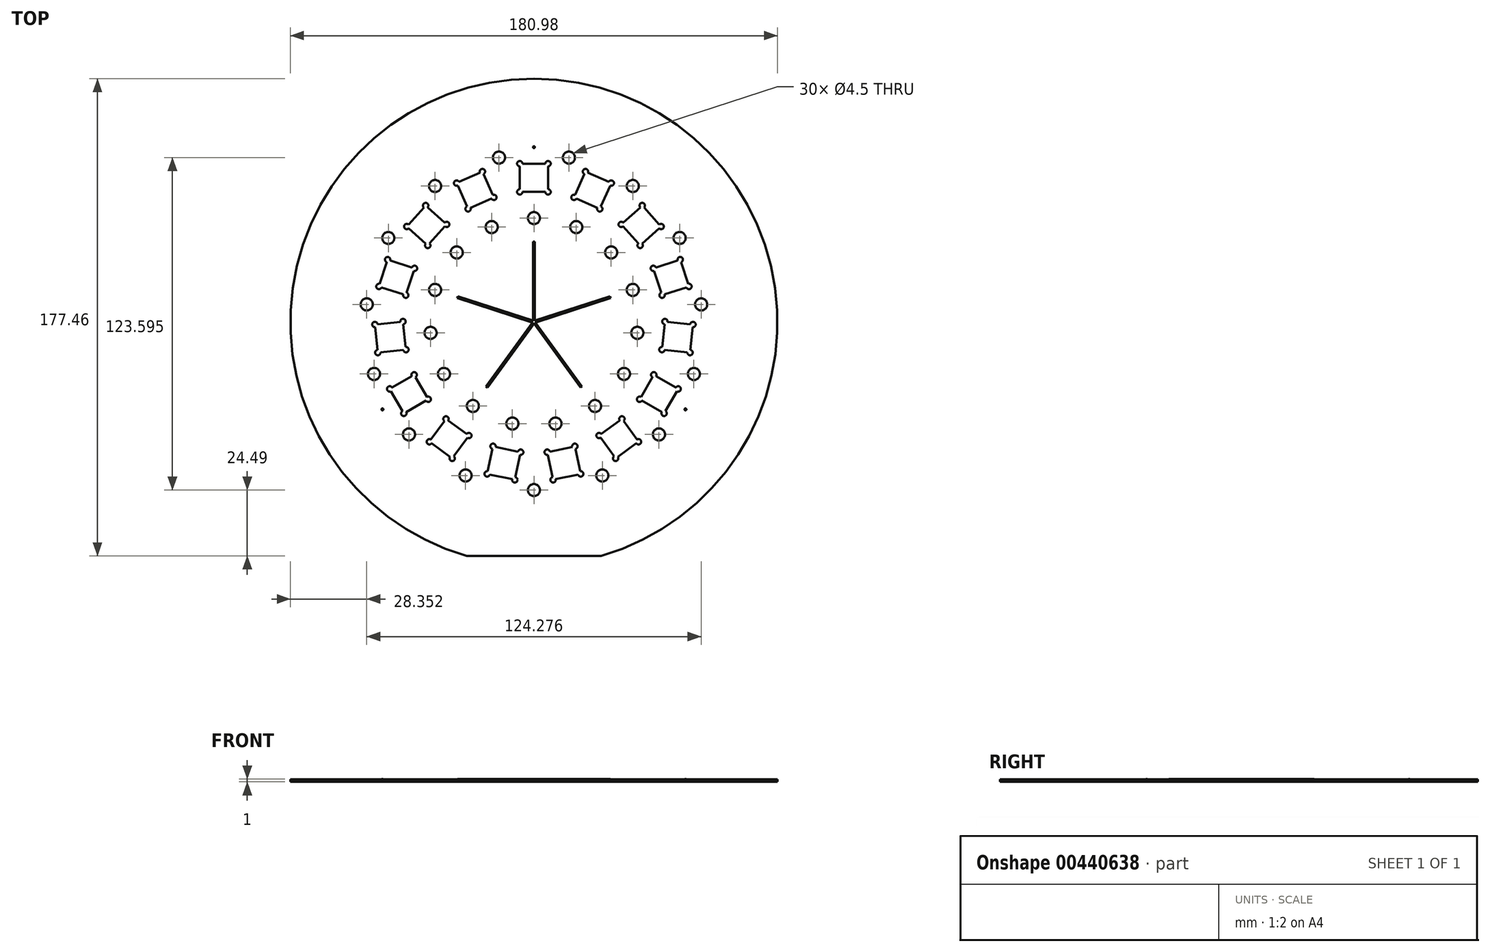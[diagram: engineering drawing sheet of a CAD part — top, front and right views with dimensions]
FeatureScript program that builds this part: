
annotation { "Feature Type Name" : "Feature", "Feature Type Description" : "" }
export const myFeature = defineFeature(function(context is Context, id is Id, definition is map)
    precondition{}
    {
        {
            var Q0;
            Q0=qCreatedBy(makeId("Top.planeOp"),FACE);
            var sketch = newSketch(context, id + "F0", { "sketchPlane" : qUnion([Q0])});
            skArc(sketch, "E0", {"start": v(25, -86.97) * mm, "mid": v(0, 90.49) * mm, "end": v(-25, -86.97) * mm});
            skCircle(sketch, "E1", {"center": v(0, 0) * mm, "radius": 53.61 * mm, "construction": true});
            skLineSegment(sketch, "E2.bottom", {"start": v(5.25, 58.86) * mm, "end": v(-5.25, 58.86) * mm});
            skLineSegment(sketch, "E2.top", {"start": v(5.25, 48.36) * mm, "end": v(-5.25, 48.36) * mm});
            skLineSegment(sketch, "E2.left", {"start": v(5.25, 58.86) * mm, "end": v(5.25, 48.36) * mm});
            skLineSegment(sketch, "E2.right", {"start": v(-5.25, 58.86) * mm, "end": v(-5.25, 48.36) * mm});
            skPoint(sketch, "E2.middle", {"position": v(0, 53.61) * mm});
            skCircle(sketch, "E3", {"center": v(0, 38.61) * mm, "radius": 2.25 * mm});
            skLineSegment(sketch, "E4", {"start": v(0, 38.61) * mm, "end": v(0, 53.61) * mm, "construction": true});
            skCircle(sketch, "E5.1.0", {"center": v(13, 61.11) * mm, "radius": 2.25 * mm, "construction": true});
            skCircle(sketch, "E5.2.0", {"center": v(-13, 61.11) * mm, "radius": 2.25 * mm});
            skCircle(sketch, "E6", {"center": v(-5.25, 58.86) * mm, "radius": 1 * mm});
            skCircle(sketch, "E7", {"center": v(5.25, 58.86) * mm, "radius": 1 * mm});
            skCircle(sketch, "E8", {"center": v(5.25, 48.36) * mm, "radius": 1 * mm});
            skCircle(sketch, "E9", {"center": v(-5.25, 48.36) * mm, "radius": 1 * mm});
            skLineSegment(sketch, "E10.1.0", {"start": v(-19.15, 55.91) * mm, "end": v(-14.88, 46.32) * mm});
            skLineSegment(sketch, "E10.1.1", {"start": v(-28.74, 51.64) * mm, "end": v(-24.47, 42.05) * mm});
            skPoint(sketch, "E10.1.2", {"position": v(-21.8, 48.98) * mm});
            skCircle(sketch, "E10.1.3", {"center": v(-15.7, 35.28) * mm, "radius": 2.25 * mm});
            skLineSegment(sketch, "E10.1.4", {"start": v(-14.88, 46.32) * mm, "end": v(-24.47, 42.05) * mm});
            skCircle(sketch, "E10.1.5", {"center": v(-13, 61.11) * mm, "radius": 2.25 * mm, "construction": true});
            skLineSegment(sketch, "E10.1.6", {"start": v(-15.7, 35.28) * mm, "end": v(-21.8, 48.98) * mm, "construction": true});
            skCircle(sketch, "E10.1.7", {"center": v(-36.72, 50.55) * mm, "radius": 2.25 * mm});
            skLineSegment(sketch, "E10.1.8", {"start": v(-19.15, 55.91) * mm, "end": v(-28.74, 51.64) * mm});
            skPoint(sketch, "E10.1.9", {"position": v(-21.8, 48.98) * mm});
            skCircle(sketch, "E10.1.10", {"center": v(-19.15, 55.91) * mm, "radius": 1 * mm});
            skCircle(sketch, "E10.1.11", {"center": v(-14.88, 46.32) * mm, "radius": 1 * mm});
            skCircle(sketch, "E10.1.12", {"center": v(-24.47, 42.05) * mm, "radius": 1 * mm});
            skCircle(sketch, "E10.1.13", {"center": v(-28.74, 51.64) * mm, "radius": 1 * mm});
            skLineSegment(sketch, "E10.2.0", {"start": v(-40.23, 43.29) * mm, "end": v(-32.43, 36.26) * mm});
            skLineSegment(sketch, "E10.2.1", {"start": v(-47.26, 35.49) * mm, "end": v(-39.46, 28.46) * mm});
            skPoint(sketch, "E10.2.2", {"position": v(-39.84, 35.88) * mm});
            skCircle(sketch, "E10.2.3", {"center": v(-28.7, 25.84) * mm, "radius": 2.25 * mm});
            skLineSegment(sketch, "E10.2.4", {"start": v(-32.43, 36.26) * mm, "end": v(-39.46, 28.46) * mm});
            skCircle(sketch, "E10.2.5", {"center": v(-36.72, 50.55) * mm, "radius": 2.25 * mm, "construction": true});
            skLineSegment(sketch, "E10.2.6", {"start": v(-28.7, 25.84) * mm, "end": v(-39.84, 35.88) * mm, "construction": true});
            skCircle(sketch, "E10.2.7", {"center": v(-54.1, 31.24) * mm, "radius": 2.25 * mm});
            skLineSegment(sketch, "E10.2.8", {"start": v(-40.23, 43.29) * mm, "end": v(-47.26, 35.49) * mm});
            skPoint(sketch, "E10.2.9", {"position": v(-39.84, 35.88) * mm});
            skCircle(sketch, "E10.2.10", {"center": v(-40.23, 43.29) * mm, "radius": 1 * mm});
            skCircle(sketch, "E10.2.11", {"center": v(-32.43, 36.26) * mm, "radius": 1 * mm});
            skCircle(sketch, "E10.2.12", {"center": v(-39.46, 28.46) * mm, "radius": 1 * mm});
            skCircle(sketch, "E10.2.13", {"center": v(-47.26, 35.49) * mm, "radius": 1 * mm});
            skLineSegment(sketch, "E11.3.3.0", {"start": v(-57.6, 13.2) * mm, "end": v(-47.62, 9.95) * mm});
            skPoint(sketch, "E11.6.3.0", {"position": v(-51, 16.57) * mm});
            skCircle(sketch, "E11.7.3.0", {"center": v(-36.72, 11.93) * mm, "radius": 2.25 * mm});
            skLineSegment(sketch, "E11.8.3.0", {"start": v(-54.36, 23.18) * mm, "end": v(-44.38, 19.94) * mm});
            skLineSegment(sketch, "E11.9.3.0", {"start": v(-44.38, 19.94) * mm, "end": v(-47.62, 9.95) * mm});
            skCircle(sketch, "E11.12.3.0", {"center": v(-54.1, 31.24) * mm, "radius": 2.25 * mm, "construction": true});
            skLineSegment(sketch, "E11.14.3.0", {"start": v(-36.72, 11.93) * mm, "end": v(-51, 16.57) * mm, "construction": true});
            skCircle(sketch, "E11.17.3.0", {"center": v(-62.14, 6.53) * mm, "radius": 2.25 * mm});
            skLineSegment(sketch, "E11.19.3.0", {"start": v(-54.36, 23.18) * mm, "end": v(-57.6, 13.2) * mm});
            skPoint(sketch, "E11.22.3.0", {"position": v(-51, 16.57) * mm});
            skCircle(sketch, "E11.23.3.0", {"center": v(-54.36, 23.18) * mm, "radius": 1 * mm});
            skCircle(sketch, "E11.25.3.0", {"center": v(-44.38, 19.94) * mm, "radius": 1 * mm});
            skCircle(sketch, "E11.27.3.0", {"center": v(-47.62, 9.95) * mm, "radius": 1 * mm});
            skCircle(sketch, "E11.29.3.0", {"center": v(-57.6, 13.2) * mm, "radius": 1 * mm});
            skLineSegment(sketch, "E11.3.4.0", {"start": v(-58, -11.37) * mm, "end": v(-47.55, -10.28) * mm});
            skPoint(sketch, "E11.6.4.0", {"position": v(-53.32, -5.6) * mm});
            skCircle(sketch, "E11.7.4.0", {"center": v(-38.4, -4.04) * mm, "radius": 2.25 * mm});
            skLineSegment(sketch, "E11.8.4.0", {"start": v(-59.1, -0.93) * mm, "end": v(-48.65, 0.17) * mm});
            skLineSegment(sketch, "E11.9.4.0", {"start": v(-48.65, 0.17) * mm, "end": v(-47.55, -10.28) * mm});
            skCircle(sketch, "E11.12.4.0", {"center": v(-62.14, 6.53) * mm, "radius": 2.25 * mm, "construction": true});
            skLineSegment(sketch, "E11.14.4.0", {"start": v(-38.4, -4.04) * mm, "end": v(-53.32, -5.6) * mm, "construction": true});
            skCircle(sketch, "E11.17.4.0", {"center": v(-59.42, -19.3) * mm, "radius": 2.25 * mm});
            skLineSegment(sketch, "E11.19.4.0", {"start": v(-59.1, -0.93) * mm, "end": v(-58, -11.37) * mm});
            skPoint(sketch, "E11.22.4.0", {"position": v(-53.32, -5.6) * mm});
            skCircle(sketch, "E11.23.4.0", {"center": v(-59.1, -0.93) * mm, "radius": 1 * mm});
            skCircle(sketch, "E11.25.4.0", {"center": v(-48.65, 0.17) * mm, "radius": 1 * mm});
            skCircle(sketch, "E11.27.4.0", {"center": v(-47.55, -10.28) * mm, "radius": 1 * mm});
            skCircle(sketch, "E11.29.4.0", {"center": v(-58, -11.37) * mm, "radius": 1 * mm});
            skLineSegment(sketch, "E11.3.5.0", {"start": v(-48.35, -33.98) * mm, "end": v(-39.26, -28.73) * mm});
            skPoint(sketch, "E11.6.5.0", {"position": v(-46.43, -26.8) * mm});
            skCircle(sketch, "E11.7.5.0", {"center": v(-33.44, -19.3) * mm, "radius": 2.25 * mm});
            skLineSegment(sketch, "E11.8.5.0", {"start": v(-53.6, -24.89) * mm, "end": v(-44.51, -19.64) * mm});
            skLineSegment(sketch, "E11.9.5.0", {"start": v(-44.51, -19.64) * mm, "end": v(-39.26, -28.73) * mm});
            skCircle(sketch, "E11.12.5.0", {"center": v(-59.42, -19.3) * mm, "radius": 2.25 * mm, "construction": true});
            skLineSegment(sketch, "E11.14.5.0", {"start": v(-33.44, -19.3) * mm, "end": v(-46.43, -26.8) * mm, "construction": true});
            skCircle(sketch, "E11.17.5.0", {"center": v(-46.43, -41.8) * mm, "radius": 2.25 * mm});
            skLineSegment(sketch, "E11.19.5.0", {"start": v(-53.6, -24.89) * mm, "end": v(-48.35, -33.98) * mm});
            skPoint(sketch, "E11.22.5.0", {"position": v(-46.43, -26.8) * mm});
            skCircle(sketch, "E11.23.5.0", {"center": v(-53.6, -24.89) * mm, "radius": 1 * mm});
            skCircle(sketch, "E11.25.5.0", {"center": v(-44.51, -19.64) * mm, "radius": 1 * mm});
            skCircle(sketch, "E11.27.5.0", {"center": v(-39.26, -28.73) * mm, "radius": 1 * mm});
            skCircle(sketch, "E11.29.5.0", {"center": v(-48.35, -33.98) * mm, "radius": 1 * mm});
            skLineSegment(sketch, "E11.3.6.0", {"start": v(-30.35, -50.7) * mm, "end": v(-24.18, -42.21) * mm});
            skPoint(sketch, "E11.6.6.0", {"position": v(-31.51, -43.38) * mm});
            skCircle(sketch, "E11.7.6.0", {"center": v(-22.7, -31.24) * mm, "radius": 2.25 * mm});
            skLineSegment(sketch, "E11.8.6.0", {"start": v(-38.85, -44.54) * mm, "end": v(-32.68, -36.04) * mm});
            skLineSegment(sketch, "E11.9.6.0", {"start": v(-32.68, -36.04) * mm, "end": v(-24.18, -42.21) * mm});
            skCircle(sketch, "E11.12.6.0", {"center": v(-46.43, -41.8) * mm, "radius": 2.25 * mm, "construction": true});
            skLineSegment(sketch, "E11.14.6.0", {"start": v(-22.7, -31.24) * mm, "end": v(-31.51, -43.38) * mm, "construction": true});
            skCircle(sketch, "E11.17.6.0", {"center": v(-25.41, -57.08) * mm, "radius": 2.25 * mm});
            skLineSegment(sketch, "E11.19.6.0", {"start": v(-38.85, -44.54) * mm, "end": v(-30.35, -50.7) * mm});
            skPoint(sketch, "E11.22.6.0", {"position": v(-31.51, -43.38) * mm});
            skCircle(sketch, "E11.23.6.0", {"center": v(-38.85, -44.54) * mm, "radius": 1 * mm});
            skCircle(sketch, "E11.25.6.0", {"center": v(-32.68, -36.04) * mm, "radius": 1 * mm});
            skCircle(sketch, "E11.27.6.0", {"center": v(-24.18, -42.21) * mm, "radius": 1 * mm});
            skCircle(sketch, "E11.29.6.0", {"center": v(-30.35, -50.7) * mm, "radius": 1 * mm});
            skLineSegment(sketch, "E11.3.7.0", {"start": v(-7.1, -58.67) * mm, "end": v(-4.92, -48.4) * mm});
            skPoint(sketch, "E11.6.7.0", {"position": v(-11.15, -52.44) * mm});
            skCircle(sketch, "E11.7.7.0", {"center": v(-8.03, -37.77) * mm, "radius": 2.25 * mm});
            skLineSegment(sketch, "E11.8.7.0", {"start": v(-17.37, -56.49) * mm, "end": v(-15.2, -46.22) * mm});
            skLineSegment(sketch, "E11.9.7.0", {"start": v(-15.2, -46.22) * mm, "end": v(-4.92, -48.4) * mm});
            skCircle(sketch, "E11.12.7.0", {"center": v(-25.41, -57.08) * mm, "radius": 2.25 * mm, "construction": true});
            skLineSegment(sketch, "E11.14.7.0", {"start": v(-8.03, -37.77) * mm, "end": v(-11.15, -52.44) * mm, "construction": true});
            skCircle(sketch, "E11.17.7.0", {"center": v(0, -62.48) * mm, "radius": 2.25 * mm});
            skLineSegment(sketch, "E11.19.7.0", {"start": v(-17.37, -56.49) * mm, "end": v(-7.1, -58.67) * mm});
            skPoint(sketch, "E11.22.7.0", {"position": v(-11.15, -52.44) * mm});
            skCircle(sketch, "E11.23.7.0", {"center": v(-17.37, -56.49) * mm, "radius": 1 * mm});
            skCircle(sketch, "E11.25.7.0", {"center": v(-15.2, -46.22) * mm, "radius": 1 * mm});
            skCircle(sketch, "E11.27.7.0", {"center": v(-4.92, -48.4) * mm, "radius": 1 * mm});
            skCircle(sketch, "E11.29.7.0", {"center": v(-7.1, -58.67) * mm, "radius": 1 * mm});
            skLineSegment(sketch, "E11.3.8.0", {"start": v(17.37, -56.49) * mm, "end": v(15.2, -46.22) * mm});
            skPoint(sketch, "E11.6.8.0", {"position": v(11.15, -52.44) * mm});
            skCircle(sketch, "E11.7.8.0", {"center": v(8.03, -37.77) * mm, "radius": 2.25 * mm});
            skLineSegment(sketch, "E11.8.8.0", {"start": v(7.1, -58.67) * mm, "end": v(4.92, -48.4) * mm});
            skLineSegment(sketch, "E11.9.8.0", {"start": v(4.92, -48.4) * mm, "end": v(15.2, -46.22) * mm});
            skCircle(sketch, "E11.12.8.0", {"center": v(0, -62.48) * mm, "radius": 2.25 * mm, "construction": true});
            skLineSegment(sketch, "E11.14.8.0", {"start": v(8.03, -37.77) * mm, "end": v(11.15, -52.44) * mm, "construction": true});
            skCircle(sketch, "E11.17.8.0", {"center": v(25.41, -57.08) * mm, "radius": 2.25 * mm});
            skLineSegment(sketch, "E11.19.8.0", {"start": v(7.1, -58.67) * mm, "end": v(17.37, -56.49) * mm});
            skPoint(sketch, "E11.22.8.0", {"position": v(11.15, -52.44) * mm});
            skCircle(sketch, "E11.23.8.0", {"center": v(7.1, -58.67) * mm, "radius": 1 * mm});
            skCircle(sketch, "E11.25.8.0", {"center": v(4.92, -48.4) * mm, "radius": 1 * mm});
            skCircle(sketch, "E11.27.8.0", {"center": v(15.2, -46.22) * mm, "radius": 1 * mm});
            skCircle(sketch, "E11.29.8.0", {"center": v(17.37, -56.49) * mm, "radius": 1 * mm});
            skLineSegment(sketch, "E11.3.9.0", {"start": v(38.85, -44.54) * mm, "end": v(32.68, -36.04) * mm});
            skPoint(sketch, "E11.6.9.0", {"position": v(31.51, -43.38) * mm});
            skCircle(sketch, "E11.7.9.0", {"center": v(22.7, -31.24) * mm, "radius": 2.25 * mm});
            skLineSegment(sketch, "E11.8.9.0", {"start": v(30.35, -50.7) * mm, "end": v(24.18, -42.21) * mm});
            skLineSegment(sketch, "E11.9.9.0", {"start": v(24.18, -42.21) * mm, "end": v(32.68, -36.04) * mm});
            skCircle(sketch, "E11.12.9.0", {"center": v(25.41, -57.08) * mm, "radius": 2.25 * mm, "construction": true});
            skLineSegment(sketch, "E11.14.9.0", {"start": v(22.7, -31.24) * mm, "end": v(31.51, -43.38) * mm, "construction": true});
            skCircle(sketch, "E11.17.9.0", {"center": v(46.43, -41.8) * mm, "radius": 2.25 * mm});
            skLineSegment(sketch, "E11.19.9.0", {"start": v(30.35, -50.7) * mm, "end": v(38.85, -44.54) * mm});
            skPoint(sketch, "E11.22.9.0", {"position": v(31.51, -43.38) * mm});
            skCircle(sketch, "E11.23.9.0", {"center": v(30.35, -50.7) * mm, "radius": 1 * mm});
            skCircle(sketch, "E11.25.9.0", {"center": v(24.18, -42.21) * mm, "radius": 1 * mm});
            skCircle(sketch, "E11.27.9.0", {"center": v(32.68, -36.04) * mm, "radius": 1 * mm});
            skCircle(sketch, "E11.29.9.0", {"center": v(38.85, -44.54) * mm, "radius": 1 * mm});
            skLineSegment(sketch, "E11.3.10.0", {"start": v(53.6, -24.89) * mm, "end": v(44.51, -19.64) * mm});
            skPoint(sketch, "E11.6.10.0", {"position": v(46.43, -26.8) * mm});
            skCircle(sketch, "E11.7.10.0", {"center": v(33.44, -19.3) * mm, "radius": 2.25 * mm});
            skLineSegment(sketch, "E11.8.10.0", {"start": v(48.35, -33.98) * mm, "end": v(39.26, -28.73) * mm});
            skLineSegment(sketch, "E11.9.10.0", {"start": v(39.26, -28.73) * mm, "end": v(44.51, -19.64) * mm});
            skCircle(sketch, "E11.12.10.0", {"center": v(46.43, -41.8) * mm, "radius": 2.25 * mm, "construction": true});
            skLineSegment(sketch, "E11.14.10.0", {"start": v(33.44, -19.3) * mm, "end": v(46.43, -26.8) * mm, "construction": true});
            skCircle(sketch, "E11.17.10.0", {"center": v(59.42, -19.3) * mm, "radius": 2.25 * mm});
            skLineSegment(sketch, "E11.19.10.0", {"start": v(48.35, -33.98) * mm, "end": v(53.6, -24.89) * mm});
            skPoint(sketch, "E11.22.10.0", {"position": v(46.43, -26.8) * mm});
            skCircle(sketch, "E11.23.10.0", {"center": v(48.35, -33.98) * mm, "radius": 1 * mm});
            skCircle(sketch, "E11.25.10.0", {"center": v(39.26, -28.73) * mm, "radius": 1 * mm});
            skCircle(sketch, "E11.27.10.0", {"center": v(44.51, -19.64) * mm, "radius": 1 * mm});
            skCircle(sketch, "E11.29.10.0", {"center": v(53.6, -24.89) * mm, "radius": 1 * mm});
            skLineSegment(sketch, "E11.3.11.0", {"start": v(59.1, -0.93) * mm, "end": v(48.65, 0.17) * mm});
            skPoint(sketch, "E11.6.11.0", {"position": v(53.32, -5.6) * mm});
            skCircle(sketch, "E11.7.11.0", {"center": v(38.4, -4.04) * mm, "radius": 2.25 * mm});
            skLineSegment(sketch, "E11.8.11.0", {"start": v(58, -11.37) * mm, "end": v(47.55, -10.28) * mm});
            skLineSegment(sketch, "E11.9.11.0", {"start": v(47.55, -10.28) * mm, "end": v(48.65, 0.17) * mm});
            skCircle(sketch, "E11.12.11.0", {"center": v(59.42, -19.3) * mm, "radius": 2.25 * mm, "construction": true});
            skLineSegment(sketch, "E11.14.11.0", {"start": v(38.4, -4.04) * mm, "end": v(53.32, -5.6) * mm, "construction": true});
            skCircle(sketch, "E11.17.11.0", {"center": v(62.14, 6.53) * mm, "radius": 2.25 * mm});
            skLineSegment(sketch, "E11.19.11.0", {"start": v(58, -11.37) * mm, "end": v(59.1, -0.93) * mm});
            skPoint(sketch, "E11.22.11.0", {"position": v(53.32, -5.6) * mm});
            skCircle(sketch, "E11.23.11.0", {"center": v(58, -11.37) * mm, "radius": 1 * mm});
            skCircle(sketch, "E11.25.11.0", {"center": v(47.55, -10.28) * mm, "radius": 1 * mm});
            skCircle(sketch, "E11.27.11.0", {"center": v(48.65, 0.17) * mm, "radius": 1 * mm});
            skCircle(sketch, "E11.29.11.0", {"center": v(59.1, -0.93) * mm, "radius": 1 * mm});
            skLineSegment(sketch, "E11.3.12.0", {"start": v(54.36, 23.18) * mm, "end": v(44.38, 19.94) * mm});
            skPoint(sketch, "E11.6.12.0", {"position": v(51, 16.57) * mm});
            skCircle(sketch, "E11.7.12.0", {"center": v(36.72, 11.93) * mm, "radius": 2.25 * mm});
            skLineSegment(sketch, "E11.8.12.0", {"start": v(57.6, 13.2) * mm, "end": v(47.62, 9.95) * mm});
            skLineSegment(sketch, "E11.9.12.0", {"start": v(47.62, 9.95) * mm, "end": v(44.38, 19.94) * mm});
            skCircle(sketch, "E11.12.12.0", {"center": v(62.14, 6.53) * mm, "radius": 2.25 * mm, "construction": true});
            skLineSegment(sketch, "E11.14.12.0", {"start": v(36.72, 11.93) * mm, "end": v(51, 16.57) * mm, "construction": true});
            skCircle(sketch, "E11.17.12.0", {"center": v(54.1, 31.24) * mm, "radius": 2.25 * mm});
            skLineSegment(sketch, "E11.19.12.0", {"start": v(57.6, 13.2) * mm, "end": v(54.36, 23.18) * mm});
            skPoint(sketch, "E11.22.12.0", {"position": v(51, 16.57) * mm});
            skCircle(sketch, "E11.23.12.0", {"center": v(57.6, 13.2) * mm, "radius": 1 * mm});
            skCircle(sketch, "E11.25.12.0", {"center": v(47.62, 9.95) * mm, "radius": 1 * mm});
            skCircle(sketch, "E11.27.12.0", {"center": v(44.38, 19.94) * mm, "radius": 1 * mm});
            skCircle(sketch, "E11.29.12.0", {"center": v(54.36, 23.18) * mm, "radius": 1 * mm});
            skLineSegment(sketch, "E11.3.13.0", {"start": v(40.23, 43.29) * mm, "end": v(32.43, 36.26) * mm});
            skPoint(sketch, "E11.6.13.0", {"position": v(39.84, 35.88) * mm});
            skCircle(sketch, "E11.7.13.0", {"center": v(28.7, 25.84) * mm, "radius": 2.25 * mm});
            skLineSegment(sketch, "E11.8.13.0", {"start": v(47.26, 35.49) * mm, "end": v(39.46, 28.46) * mm});
            skLineSegment(sketch, "E11.9.13.0", {"start": v(39.46, 28.46) * mm, "end": v(32.43, 36.26) * mm});
            skCircle(sketch, "E11.12.13.0", {"center": v(54.1, 31.24) * mm, "radius": 2.25 * mm, "construction": true});
            skLineSegment(sketch, "E11.14.13.0", {"start": v(28.7, 25.84) * mm, "end": v(39.84, 35.88) * mm, "construction": true});
            skCircle(sketch, "E11.17.13.0", {"center": v(36.72, 50.55) * mm, "radius": 2.25 * mm});
            skLineSegment(sketch, "E11.19.13.0", {"start": v(47.26, 35.49) * mm, "end": v(40.23, 43.29) * mm});
            skPoint(sketch, "E11.22.13.0", {"position": v(39.84, 35.88) * mm});
            skCircle(sketch, "E11.23.13.0", {"center": v(47.26, 35.49) * mm, "radius": 1 * mm});
            skCircle(sketch, "E11.25.13.0", {"center": v(39.46, 28.46) * mm, "radius": 1 * mm});
            skCircle(sketch, "E11.27.13.0", {"center": v(32.43, 36.26) * mm, "radius": 1 * mm});
            skCircle(sketch, "E11.29.13.0", {"center": v(40.23, 43.29) * mm, "radius": 1 * mm});
            skLineSegment(sketch, "E11.3.14.0", {"start": v(19.15, 55.91) * mm, "end": v(14.88, 46.32) * mm});
            skPoint(sketch, "E11.6.14.0", {"position": v(21.8, 48.98) * mm});
            skCircle(sketch, "E11.7.14.0", {"center": v(15.7, 35.28) * mm, "radius": 2.25 * mm});
            skLineSegment(sketch, "E11.8.14.0", {"start": v(28.74, 51.64) * mm, "end": v(24.47, 42.05) * mm});
            skLineSegment(sketch, "E11.9.14.0", {"start": v(24.47, 42.05) * mm, "end": v(14.88, 46.32) * mm});
            skCircle(sketch, "E11.12.14.0", {"center": v(36.72, 50.55) * mm, "radius": 2.25 * mm, "construction": true});
            skLineSegment(sketch, "E11.14.14.0", {"start": v(15.7, 35.28) * mm, "end": v(21.8, 48.98) * mm, "construction": true});
            skCircle(sketch, "E11.17.14.0", {"center": v(13, 61.11) * mm, "radius": 2.25 * mm});
            skLineSegment(sketch, "E11.19.14.0", {"start": v(28.74, 51.64) * mm, "end": v(19.15, 55.91) * mm});
            skPoint(sketch, "E11.22.14.0", {"position": v(21.8, 48.98) * mm});
            skCircle(sketch, "E11.23.14.0", {"center": v(28.74, 51.64) * mm, "radius": 1 * mm});
            skCircle(sketch, "E11.25.14.0", {"center": v(24.47, 42.05) * mm, "radius": 1 * mm});
            skCircle(sketch, "E11.27.14.0", {"center": v(14.88, 46.32) * mm, "radius": 1 * mm});
            skCircle(sketch, "E11.29.14.0", {"center": v(19.15, 55.91) * mm, "radius": 1 * mm});
            skLineSegment(sketch, "E12", {"start": v(-25, -86.97) * mm, "end": v(25, -86.97) * mm});
            skPoint(sketch, "E13.endSnap0", {"position": v(9.59, -45.1) * mm});
            skLineSegment(sketch, "E14", {"start": v(0, 0) * mm, "end": v(0, -86.97) * mm, "construction": true});
            skSolve(sketch);
        }
        {
            var Q0;
            Q0=qSketchRegion(id+"F0",true);
            extrude(context, id + "F1", {"entities" : qUnion([Q0]), "depth" : 1 * mm});
        }
        {
            var Q0;
            Q0=makeQuery(id+"F1.opExtrude","CAP_FACE",FACE,{"disambiguationData":[OSD([sQuery(id+"F0.wireOp",EDGE,"E0"),sQuery(id+"F0.wireOp",EDGE,"E2.bottom"),sQuery(id+"F0.wireOp",EDGE,"E2.top"),sQuery(id+"F0.wireOp",EDGE,"E2.left"),sQuery(id+"F0.wireOp",EDGE,"E2.right"),sQuery(id+"F0.wireOp",EDGE,"E3"),sQuery(id+"F0.wireOp",EDGE,"E5.2.0"),sQuery(id+"F0.wireOp",EDGE,"E6"),sQuery(id+"F0.wireOp",EDGE,"E7"),sQuery(id+"F0.wireOp",EDGE,"E8"),sQuery(id+"F0.wireOp",EDGE,"E9"),sQuery(id+"F0.wireOp",EDGE,"E10.1.0"),sQuery(id+"F0.wireOp",EDGE,"E10.1.1"),sQuery(id+"F0.wireOp",EDGE,"E10.1.3"),sQuery(id+"F0.wireOp",EDGE,"E10.1.4"),sQuery(id+"F0.wireOp",EDGE,"E10.1.7"),sQuery(id+"F0.wireOp",EDGE,"E10.1.8"),sQuery(id+"F0.wireOp",EDGE,"E10.1.10"),sQuery(id+"F0.wireOp",EDGE,"E10.1.11"),sQuery(id+"F0.wireOp",EDGE,"E10.1.12"),sQuery(id+"F0.wireOp",EDGE,"E10.1.13"),sQuery(id+"F0.wireOp",EDGE,"E10.2.0"),sQuery(id+"F0.wireOp",EDGE,"E10.2.1"),sQuery(id+"F0.wireOp",EDGE,"E10.2.3"),sQuery(id+"F0.wireOp",EDGE,"E10.2.4"),sQuery(id+"F0.wireOp",EDGE,"E10.2.7"),sQuery(id+"F0.wireOp",EDGE,"E10.2.8"),sQuery(id+"F0.wireOp",EDGE,"E10.2.10"),sQuery(id+"F0.wireOp",EDGE,"E10.2.11"),sQuery(id+"F0.wireOp",EDGE,"E10.2.12"),sQuery(id+"F0.wireOp",EDGE,"E10.2.13"),sQuery(id+"F0.wireOp",EDGE,"E11.3.3.0"),sQuery(id+"F0.wireOp",EDGE,"E11.7.3.0"),sQuery(id+"F0.wireOp",EDGE,"E11.8.3.0"),sQuery(id+"F0.wireOp",EDGE,"E11.9.3.0"),sQuery(id+"F0.wireOp",EDGE,"E11.17.3.0"),sQuery(id+"F0.wireOp",EDGE,"E11.19.3.0"),sQuery(id+"F0.wireOp",EDGE,"E11.23.3.0"),sQuery(id+"F0.wireOp",EDGE,"E11.25.3.0"),sQuery(id+"F0.wireOp",EDGE,"E11.27.3.0"),sQuery(id+"F0.wireOp",EDGE,"E11.29.3.0"),sQuery(id+"F0.wireOp",EDGE,"E11.3.4.0"),sQuery(id+"F0.wireOp",EDGE,"E11.7.4.0"),sQuery(id+"F0.wireOp",EDGE,"E11.8.4.0"),sQuery(id+"F0.wireOp",EDGE,"E11.9.4.0"),sQuery(id+"F0.wireOp",EDGE,"E11.17.4.0"),sQuery(id+"F0.wireOp",EDGE,"E11.19.4.0"),sQuery(id+"F0.wireOp",EDGE,"E11.23.4.0"),sQuery(id+"F0.wireOp",EDGE,"E11.25.4.0"),sQuery(id+"F0.wireOp",EDGE,"E11.27.4.0"),sQuery(id+"F0.wireOp",EDGE,"E11.29.4.0"),sQuery(id+"F0.wireOp",EDGE,"E11.3.5.0"),sQuery(id+"F0.wireOp",EDGE,"E11.7.5.0"),sQuery(id+"F0.wireOp",EDGE,"E11.8.5.0"),sQuery(id+"F0.wireOp",EDGE,"E11.9.5.0"),sQuery(id+"F0.wireOp",EDGE,"E11.17.5.0"),sQuery(id+"F0.wireOp",EDGE,"E11.19.5.0"),sQuery(id+"F0.wireOp",EDGE,"E11.23.5.0"),sQuery(id+"F0.wireOp",EDGE,"E11.25.5.0"),sQuery(id+"F0.wireOp",EDGE,"E11.27.5.0"),sQuery(id+"F0.wireOp",EDGE,"E11.29.5.0"),sQuery(id+"F0.wireOp",EDGE,"E11.3.6.0"),sQuery(id+"F0.wireOp",EDGE,"E11.7.6.0"),sQuery(id+"F0.wireOp",EDGE,"E11.8.6.0"),sQuery(id+"F0.wireOp",EDGE,"E11.9.6.0"),sQuery(id+"F0.wireOp",EDGE,"E11.17.6.0"),sQuery(id+"F0.wireOp",EDGE,"E11.19.6.0"),sQuery(id+"F0.wireOp",EDGE,"E11.23.6.0"),sQuery(id+"F0.wireOp",EDGE,"E11.25.6.0"),sQuery(id+"F0.wireOp",EDGE,"E11.27.6.0"),sQuery(id+"F0.wireOp",EDGE,"E11.29.6.0"),sQuery(id+"F0.wireOp",EDGE,"E11.3.7.0"),sQuery(id+"F0.wireOp",EDGE,"E11.7.7.0"),sQuery(id+"F0.wireOp",EDGE,"E11.8.7.0"),sQuery(id+"F0.wireOp",EDGE,"E11.9.7.0"),sQuery(id+"F0.wireOp",EDGE,"E11.17.7.0"),sQuery(id+"F0.wireOp",EDGE,"E11.19.7.0"),sQuery(id+"F0.wireOp",EDGE,"E11.23.7.0"),sQuery(id+"F0.wireOp",EDGE,"E11.25.7.0"),sQuery(id+"F0.wireOp",EDGE,"E11.27.7.0"),sQuery(id+"F0.wireOp",EDGE,"E11.29.7.0"),sQuery(id+"F0.wireOp",EDGE,"E11.3.8.0"),sQuery(id+"F0.wireOp",EDGE,"E11.7.8.0"),sQuery(id+"F0.wireOp",EDGE,"E11.8.8.0"),sQuery(id+"F0.wireOp",EDGE,"E11.9.8.0"),sQuery(id+"F0.wireOp",EDGE,"E11.17.8.0"),sQuery(id+"F0.wireOp",EDGE,"E11.19.8.0"),sQuery(id+"F0.wireOp",EDGE,"E11.23.8.0"),sQuery(id+"F0.wireOp",EDGE,"E11.25.8.0"),sQuery(id+"F0.wireOp",EDGE,"E11.27.8.0"),sQuery(id+"F0.wireOp",EDGE,"E11.29.8.0"),sQuery(id+"F0.wireOp",EDGE,"E11.3.9.0"),sQuery(id+"F0.wireOp",EDGE,"E11.7.9.0"),sQuery(id+"F0.wireOp",EDGE,"E11.8.9.0"),sQuery(id+"F0.wireOp",EDGE,"E11.9.9.0"),sQuery(id+"F0.wireOp",EDGE,"E11.17.9.0"),sQuery(id+"F0.wireOp",EDGE,"E11.19.9.0"),sQuery(id+"F0.wireOp",EDGE,"E11.23.9.0"),sQuery(id+"F0.wireOp",EDGE,"E11.25.9.0"),sQuery(id+"F0.wireOp",EDGE,"E11.27.9.0"),sQuery(id+"F0.wireOp",EDGE,"E11.29.9.0"),sQuery(id+"F0.wireOp",EDGE,"E11.3.10.0"),sQuery(id+"F0.wireOp",EDGE,"E11.7.10.0"),sQuery(id+"F0.wireOp",EDGE,"E11.8.10.0"),sQuery(id+"F0.wireOp",EDGE,"E11.9.10.0"),sQuery(id+"F0.wireOp",EDGE,"E11.17.10.0"),sQuery(id+"F0.wireOp",EDGE,"E11.19.10.0"),sQuery(id+"F0.wireOp",EDGE,"E11.23.10.0"),sQuery(id+"F0.wireOp",EDGE,"E11.25.10.0"),sQuery(id+"F0.wireOp",EDGE,"E11.27.10.0"),sQuery(id+"F0.wireOp",EDGE,"E11.29.10.0"),sQuery(id+"F0.wireOp",EDGE,"E11.3.11.0"),sQuery(id+"F0.wireOp",EDGE,"E11.7.11.0"),sQuery(id+"F0.wireOp",EDGE,"E11.8.11.0"),sQuery(id+"F0.wireOp",EDGE,"E11.9.11.0"),sQuery(id+"F0.wireOp",EDGE,"E11.17.11.0"),sQuery(id+"F0.wireOp",EDGE,"E11.19.11.0"),sQuery(id+"F0.wireOp",EDGE,"E11.23.11.0"),sQuery(id+"F0.wireOp",EDGE,"E11.25.11.0"),sQuery(id+"F0.wireOp",EDGE,"E11.27.11.0"),sQuery(id+"F0.wireOp",EDGE,"E11.29.11.0"),sQuery(id+"F0.wireOp",EDGE,"E11.3.12.0"),sQuery(id+"F0.wireOp",EDGE,"E11.7.12.0"),sQuery(id+"F0.wireOp",EDGE,"E11.8.12.0"),sQuery(id+"F0.wireOp",EDGE,"E11.9.12.0"),sQuery(id+"F0.wireOp",EDGE,"E11.17.12.0"),sQuery(id+"F0.wireOp",EDGE,"E11.19.12.0"),sQuery(id+"F0.wireOp",EDGE,"E11.23.12.0"),sQuery(id+"F0.wireOp",EDGE,"E11.25.12.0"),sQuery(id+"F0.wireOp",EDGE,"E11.27.12.0"),sQuery(id+"F0.wireOp",EDGE,"E11.29.12.0"),sQuery(id+"F0.wireOp",EDGE,"E11.3.13.0"),sQuery(id+"F0.wireOp",EDGE,"E11.7.13.0"),sQuery(id+"F0.wireOp",EDGE,"E11.8.13.0"),sQuery(id+"F0.wireOp",EDGE,"E11.9.13.0"),sQuery(id+"F0.wireOp",EDGE,"E11.17.13.0"),sQuery(id+"F0.wireOp",EDGE,"E11.19.13.0"),sQuery(id+"F0.wireOp",EDGE,"E11.23.13.0"),sQuery(id+"F0.wireOp",EDGE,"E11.25.13.0"),sQuery(id+"F0.wireOp",EDGE,"E11.27.13.0"),sQuery(id+"F0.wireOp",EDGE,"E11.29.13.0"),sQuery(id+"F0.wireOp",EDGE,"E11.3.14.0"),sQuery(id+"F0.wireOp",EDGE,"E11.7.14.0"),sQuery(id+"F0.wireOp",EDGE,"E11.8.14.0"),sQuery(id+"F0.wireOp",EDGE,"E11.9.14.0"),sQuery(id+"F0.wireOp",EDGE,"E11.17.14.0"),sQuery(id+"F0.wireOp",EDGE,"E11.19.14.0"),sQuery(id+"F0.wireOp",EDGE,"E11.23.14.0"),sQuery(id+"F0.wireOp",EDGE,"E11.25.14.0"),sQuery(id+"F0.wireOp",EDGE,"E11.27.14.0"),sQuery(id+"F0.wireOp",EDGE,"E11.29.14.0"),sQuery(id+"F0.wireOp",EDGE,"E11.3.15.0"),sQuery(id+"F0.wireOp",EDGE,"E11.7.15.0"),sQuery(id+"F0.wireOp",EDGE,"E11.8.15.0"),sQuery(id+"F0.wireOp",EDGE,"E11.9.15.0"),sQuery(id+"F0.wireOp",EDGE,"E11.17.15.0"),sQuery(id+"F0.wireOp",EDGE,"E11.19.15.0"),sQuery(id+"F0.wireOp",EDGE,"E11.23.15.0"),sQuery(id+"F0.wireOp",EDGE,"E11.25.15.0"),sQuery(id+"F0.wireOp",EDGE,"E11.27.15.0"),sQuery(id+"F0.wireOp",EDGE,"E11.29.15.0"),sQuery(id+"F0.wireOp",EDGE,"E12")])],"isStart":false});
            var sketch = newSketch(context, id + "F2", { "sketchPlane" : qUnion([Q0])});
            skLineSegment(sketch, "E15.bottom", {"start": v(-0.5, 0) * mm, "end": v(0.5, 0) * mm});
            skLineSegment(sketch, "E15.top", {"start": v(-0.5, 30) * mm, "end": v(0.5, 30) * mm});
            skLineSegment(sketch, "E15.left", {"start": v(-0.5, 0) * mm, "end": v(-0.5, 30) * mm});
            skLineSegment(sketch, "E15.right", {"start": v(0.5, 0) * mm, "end": v(0.5, 30) * mm});
            skLineSegment(sketch, "E16.1.0", {"start": v(-0.15, -0.48) * mm, "end": v(-28.69, 8.8) * mm});
            skLineSegment(sketch, "E16.1.1", {"start": v(0.15, 0.48) * mm, "end": v(-28.38, 9.75) * mm});
            skLineSegment(sketch, "E16.1.2", {"start": v(-0.15, -0.48) * mm, "end": v(0.15, 0.48) * mm});
            skLineSegment(sketch, "E16.1.3", {"start": v(-28.69, 8.8) * mm, "end": v(-28.38, 9.75) * mm});
            skLineSegment(sketch, "E16.2.0", {"start": v(0.4, -0.3) * mm, "end": v(-17.23, -24.56) * mm});
            skLineSegment(sketch, "E16.2.1", {"start": v(-0.4, 0.3) * mm, "end": v(-18.04, -23.98) * mm});
            skLineSegment(sketch, "E16.2.2", {"start": v(0.4, -0.3) * mm, "end": v(-0.4, 0.3) * mm});
            skLineSegment(sketch, "E16.2.3", {"start": v(-17.23, -24.56) * mm, "end": v(-18.04, -23.98) * mm});
            skPoint(sketch, "E16.center", {"position": v(0, 0) * mm});
            skLineSegment(sketch, "E17.1.3.0", {"start": v(0.4, 0.3) * mm, "end": v(18.04, -23.98) * mm});
            skLineSegment(sketch, "E17.3.3.0", {"start": v(-0.4, -0.3) * mm, "end": v(17.23, -24.56) * mm});
            skLineSegment(sketch, "E17.6.3.0", {"start": v(0.4, 0.3) * mm, "end": v(-0.4, -0.3) * mm});
            skLineSegment(sketch, "E17.9.3.0", {"start": v(18.04, -23.98) * mm, "end": v(17.23, -24.56) * mm});
            skLineSegment(sketch, "E18.1.4.0", {"start": v(-0.15, 0.48) * mm, "end": v(28.38, 9.75) * mm});
            skLineSegment(sketch, "E18.3.4.0", {"start": v(0.15, -0.48) * mm, "end": v(28.69, 8.8) * mm});
            skLineSegment(sketch, "E18.6.4.0", {"start": v(-0.15, 0.48) * mm, "end": v(0.15, -0.48) * mm});
            skLineSegment(sketch, "E18.9.4.0", {"start": v(28.38, 9.75) * mm, "end": v(28.69, 8.8) * mm});
            skCircle(sketch, "E19", {"center": v(0, 65) * mm, "radius": 0.5 * mm});
            skCircle(sketch, "E20.1.0", {"center": v(-56.3, -32.5) * mm, "radius": 0.5 * mm});
            skCircle(sketch, "E20.2.0", {"center": v(56.3, -32.5) * mm, "radius": 0.5 * mm});
            skSolve(sketch);
        }
        {
            var Q0;
            {var subQ15=sQuery(id+"F2.wireOp",EDGE,"E15.top");Q0=makeQuery(id+"F2.imprint","IMPRINT",FACE,{"disambiguationData":[TD([[makeQuery(id+"F2.imprint","IMPRINT",EDGE,{"derivedFrom":subQ15}),1.0]])]});}
            extrude(context, id + "F3", {"entities" : qUnion([Q0]), "operationType" : NewBodyOperationType.REMOVE, "oppositeDirection" : true, "depth" : .1 * mm});
        }
        {
            var Q0;
            Q0=makeQuery(id+"F1.opExtrude","CAP_FACE",FACE,{"disambiguationData":[OSD([sQuery(id+"F0.wireOp",EDGE,"E0"),sQuery(id+"F0.wireOp",EDGE,"E2.bottom"),sQuery(id+"F0.wireOp",EDGE,"E2.top"),sQuery(id+"F0.wireOp",EDGE,"E2.left"),sQuery(id+"F0.wireOp",EDGE,"E2.right"),sQuery(id+"F0.wireOp",EDGE,"E3"),sQuery(id+"F0.wireOp",EDGE,"E5.2.0"),sQuery(id+"F0.wireOp",EDGE,"E6"),sQuery(id+"F0.wireOp",EDGE,"E7"),sQuery(id+"F0.wireOp",EDGE,"E8"),sQuery(id+"F0.wireOp",EDGE,"E9"),sQuery(id+"F0.wireOp",EDGE,"E10.1.0"),sQuery(id+"F0.wireOp",EDGE,"E10.1.1"),sQuery(id+"F0.wireOp",EDGE,"E10.1.3"),sQuery(id+"F0.wireOp",EDGE,"E10.1.4"),sQuery(id+"F0.wireOp",EDGE,"E10.1.7"),sQuery(id+"F0.wireOp",EDGE,"E10.1.8"),sQuery(id+"F0.wireOp",EDGE,"E10.1.10"),sQuery(id+"F0.wireOp",EDGE,"E10.1.11"),sQuery(id+"F0.wireOp",EDGE,"E10.1.12"),sQuery(id+"F0.wireOp",EDGE,"E10.1.13"),sQuery(id+"F0.wireOp",EDGE,"E10.2.0"),sQuery(id+"F0.wireOp",EDGE,"E10.2.1"),sQuery(id+"F0.wireOp",EDGE,"E10.2.3"),sQuery(id+"F0.wireOp",EDGE,"E10.2.4"),sQuery(id+"F0.wireOp",EDGE,"E10.2.7"),sQuery(id+"F0.wireOp",EDGE,"E10.2.8"),sQuery(id+"F0.wireOp",EDGE,"E10.2.10"),sQuery(id+"F0.wireOp",EDGE,"E10.2.11"),sQuery(id+"F0.wireOp",EDGE,"E10.2.12"),sQuery(id+"F0.wireOp",EDGE,"E10.2.13"),sQuery(id+"F0.wireOp",EDGE,"E11.3.3.0"),sQuery(id+"F0.wireOp",EDGE,"E11.7.3.0"),sQuery(id+"F0.wireOp",EDGE,"E11.8.3.0"),sQuery(id+"F0.wireOp",EDGE,"E11.9.3.0"),sQuery(id+"F0.wireOp",EDGE,"E11.17.3.0"),sQuery(id+"F0.wireOp",EDGE,"E11.19.3.0"),sQuery(id+"F0.wireOp",EDGE,"E11.23.3.0"),sQuery(id+"F0.wireOp",EDGE,"E11.25.3.0"),sQuery(id+"F0.wireOp",EDGE,"E11.27.3.0"),sQuery(id+"F0.wireOp",EDGE,"E11.29.3.0"),sQuery(id+"F0.wireOp",EDGE,"E11.3.4.0"),sQuery(id+"F0.wireOp",EDGE,"E11.7.4.0"),sQuery(id+"F0.wireOp",EDGE,"E11.8.4.0"),sQuery(id+"F0.wireOp",EDGE,"E11.9.4.0"),sQuery(id+"F0.wireOp",EDGE,"E11.17.4.0"),sQuery(id+"F0.wireOp",EDGE,"E11.19.4.0"),sQuery(id+"F0.wireOp",EDGE,"E11.23.4.0"),sQuery(id+"F0.wireOp",EDGE,"E11.25.4.0"),sQuery(id+"F0.wireOp",EDGE,"E11.27.4.0"),sQuery(id+"F0.wireOp",EDGE,"E11.29.4.0"),sQuery(id+"F0.wireOp",EDGE,"E11.3.5.0"),sQuery(id+"F0.wireOp",EDGE,"E11.7.5.0"),sQuery(id+"F0.wireOp",EDGE,"E11.8.5.0"),sQuery(id+"F0.wireOp",EDGE,"E11.9.5.0"),sQuery(id+"F0.wireOp",EDGE,"E11.17.5.0"),sQuery(id+"F0.wireOp",EDGE,"E11.19.5.0"),sQuery(id+"F0.wireOp",EDGE,"E11.23.5.0"),sQuery(id+"F0.wireOp",EDGE,"E11.25.5.0"),sQuery(id+"F0.wireOp",EDGE,"E11.27.5.0"),sQuery(id+"F0.wireOp",EDGE,"E11.29.5.0"),sQuery(id+"F0.wireOp",EDGE,"E11.3.6.0"),sQuery(id+"F0.wireOp",EDGE,"E11.7.6.0"),sQuery(id+"F0.wireOp",EDGE,"E11.8.6.0"),sQuery(id+"F0.wireOp",EDGE,"E11.9.6.0"),sQuery(id+"F0.wireOp",EDGE,"E11.17.6.0"),sQuery(id+"F0.wireOp",EDGE,"E11.19.6.0"),sQuery(id+"F0.wireOp",EDGE,"E11.23.6.0"),sQuery(id+"F0.wireOp",EDGE,"E11.25.6.0"),sQuery(id+"F0.wireOp",EDGE,"E11.27.6.0"),sQuery(id+"F0.wireOp",EDGE,"E11.29.6.0"),sQuery(id+"F0.wireOp",EDGE,"E11.3.7.0"),sQuery(id+"F0.wireOp",EDGE,"E11.7.7.0"),sQuery(id+"F0.wireOp",EDGE,"E11.8.7.0"),sQuery(id+"F0.wireOp",EDGE,"E11.9.7.0"),sQuery(id+"F0.wireOp",EDGE,"E11.17.7.0"),sQuery(id+"F0.wireOp",EDGE,"E11.19.7.0"),sQuery(id+"F0.wireOp",EDGE,"E11.23.7.0"),sQuery(id+"F0.wireOp",EDGE,"E11.25.7.0"),sQuery(id+"F0.wireOp",EDGE,"E11.27.7.0"),sQuery(id+"F0.wireOp",EDGE,"E11.29.7.0"),sQuery(id+"F0.wireOp",EDGE,"E11.3.8.0"),sQuery(id+"F0.wireOp",EDGE,"E11.7.8.0"),sQuery(id+"F0.wireOp",EDGE,"E11.8.8.0"),sQuery(id+"F0.wireOp",EDGE,"E11.9.8.0"),sQuery(id+"F0.wireOp",EDGE,"E11.17.8.0"),sQuery(id+"F0.wireOp",EDGE,"E11.19.8.0"),sQuery(id+"F0.wireOp",EDGE,"E11.23.8.0"),sQuery(id+"F0.wireOp",EDGE,"E11.25.8.0"),sQuery(id+"F0.wireOp",EDGE,"E11.27.8.0"),sQuery(id+"F0.wireOp",EDGE,"E11.29.8.0"),sQuery(id+"F0.wireOp",EDGE,"E11.3.9.0"),sQuery(id+"F0.wireOp",EDGE,"E11.7.9.0"),sQuery(id+"F0.wireOp",EDGE,"E11.8.9.0"),sQuery(id+"F0.wireOp",EDGE,"E11.9.9.0"),sQuery(id+"F0.wireOp",EDGE,"E11.17.9.0"),sQuery(id+"F0.wireOp",EDGE,"E11.19.9.0"),sQuery(id+"F0.wireOp",EDGE,"E11.23.9.0"),sQuery(id+"F0.wireOp",EDGE,"E11.25.9.0"),sQuery(id+"F0.wireOp",EDGE,"E11.27.9.0"),sQuery(id+"F0.wireOp",EDGE,"E11.29.9.0"),sQuery(id+"F0.wireOp",EDGE,"E11.3.10.0"),sQuery(id+"F0.wireOp",EDGE,"E11.7.10.0"),sQuery(id+"F0.wireOp",EDGE,"E11.8.10.0"),sQuery(id+"F0.wireOp",EDGE,"E11.9.10.0"),sQuery(id+"F0.wireOp",EDGE,"E11.17.10.0"),sQuery(id+"F0.wireOp",EDGE,"E11.19.10.0"),sQuery(id+"F0.wireOp",EDGE,"E11.23.10.0"),sQuery(id+"F0.wireOp",EDGE,"E11.25.10.0"),sQuery(id+"F0.wireOp",EDGE,"E11.27.10.0"),sQuery(id+"F0.wireOp",EDGE,"E11.29.10.0"),sQuery(id+"F0.wireOp",EDGE,"E11.3.11.0"),sQuery(id+"F0.wireOp",EDGE,"E11.7.11.0"),sQuery(id+"F0.wireOp",EDGE,"E11.8.11.0"),sQuery(id+"F0.wireOp",EDGE,"E11.9.11.0"),sQuery(id+"F0.wireOp",EDGE,"E11.17.11.0"),sQuery(id+"F0.wireOp",EDGE,"E11.19.11.0"),sQuery(id+"F0.wireOp",EDGE,"E11.23.11.0"),sQuery(id+"F0.wireOp",EDGE,"E11.25.11.0"),sQuery(id+"F0.wireOp",EDGE,"E11.27.11.0"),sQuery(id+"F0.wireOp",EDGE,"E11.29.11.0"),sQuery(id+"F0.wireOp",EDGE,"E11.3.12.0"),sQuery(id+"F0.wireOp",EDGE,"E11.7.12.0"),sQuery(id+"F0.wireOp",EDGE,"E11.8.12.0"),sQuery(id+"F0.wireOp",EDGE,"E11.9.12.0"),sQuery(id+"F0.wireOp",EDGE,"E11.17.12.0"),sQuery(id+"F0.wireOp",EDGE,"E11.19.12.0"),sQuery(id+"F0.wireOp",EDGE,"E11.23.12.0"),sQuery(id+"F0.wireOp",EDGE,"E11.25.12.0"),sQuery(id+"F0.wireOp",EDGE,"E11.27.12.0"),sQuery(id+"F0.wireOp",EDGE,"E11.29.12.0"),sQuery(id+"F0.wireOp",EDGE,"E11.3.13.0"),sQuery(id+"F0.wireOp",EDGE,"E11.7.13.0"),sQuery(id+"F0.wireOp",EDGE,"E11.8.13.0"),sQuery(id+"F0.wireOp",EDGE,"E11.9.13.0"),sQuery(id+"F0.wireOp",EDGE,"E11.17.13.0"),sQuery(id+"F0.wireOp",EDGE,"E11.19.13.0"),sQuery(id+"F0.wireOp",EDGE,"E11.23.13.0"),sQuery(id+"F0.wireOp",EDGE,"E11.25.13.0"),sQuery(id+"F0.wireOp",EDGE,"E11.27.13.0"),sQuery(id+"F0.wireOp",EDGE,"E11.29.13.0"),sQuery(id+"F0.wireOp",EDGE,"E11.3.14.0"),sQuery(id+"F0.wireOp",EDGE,"E11.7.14.0"),sQuery(id+"F0.wireOp",EDGE,"E11.8.14.0"),sQuery(id+"F0.wireOp",EDGE,"E11.9.14.0"),sQuery(id+"F0.wireOp",EDGE,"E11.17.14.0"),sQuery(id+"F0.wireOp",EDGE,"E11.19.14.0"),sQuery(id+"F0.wireOp",EDGE,"E11.23.14.0"),sQuery(id+"F0.wireOp",EDGE,"E11.25.14.0"),sQuery(id+"F0.wireOp",EDGE,"E11.27.14.0"),sQuery(id+"F0.wireOp",EDGE,"E11.29.14.0"),sQuery(id+"F0.wireOp",EDGE,"E11.3.15.0"),sQuery(id+"F0.wireOp",EDGE,"E11.7.15.0"),sQuery(id+"F0.wireOp",EDGE,"E11.8.15.0"),sQuery(id+"F0.wireOp",EDGE,"E11.9.15.0"),sQuery(id+"F0.wireOp",EDGE,"E11.17.15.0"),sQuery(id+"F0.wireOp",EDGE,"E11.19.15.0"),sQuery(id+"F0.wireOp",EDGE,"E11.23.15.0"),sQuery(id+"F0.wireOp",EDGE,"E11.25.15.0"),sQuery(id+"F0.wireOp",EDGE,"E11.27.15.0"),sQuery(id+"F0.wireOp",EDGE,"E11.29.15.0"),sQuery(id+"F0.wireOp",EDGE,"E12")])],"isStart":false});
            chamfer(context, id + "F4", {"entities" : qUnion([Q0]), "width" : .25 * mm, "tangentPropagation" : true});
        }
    });
